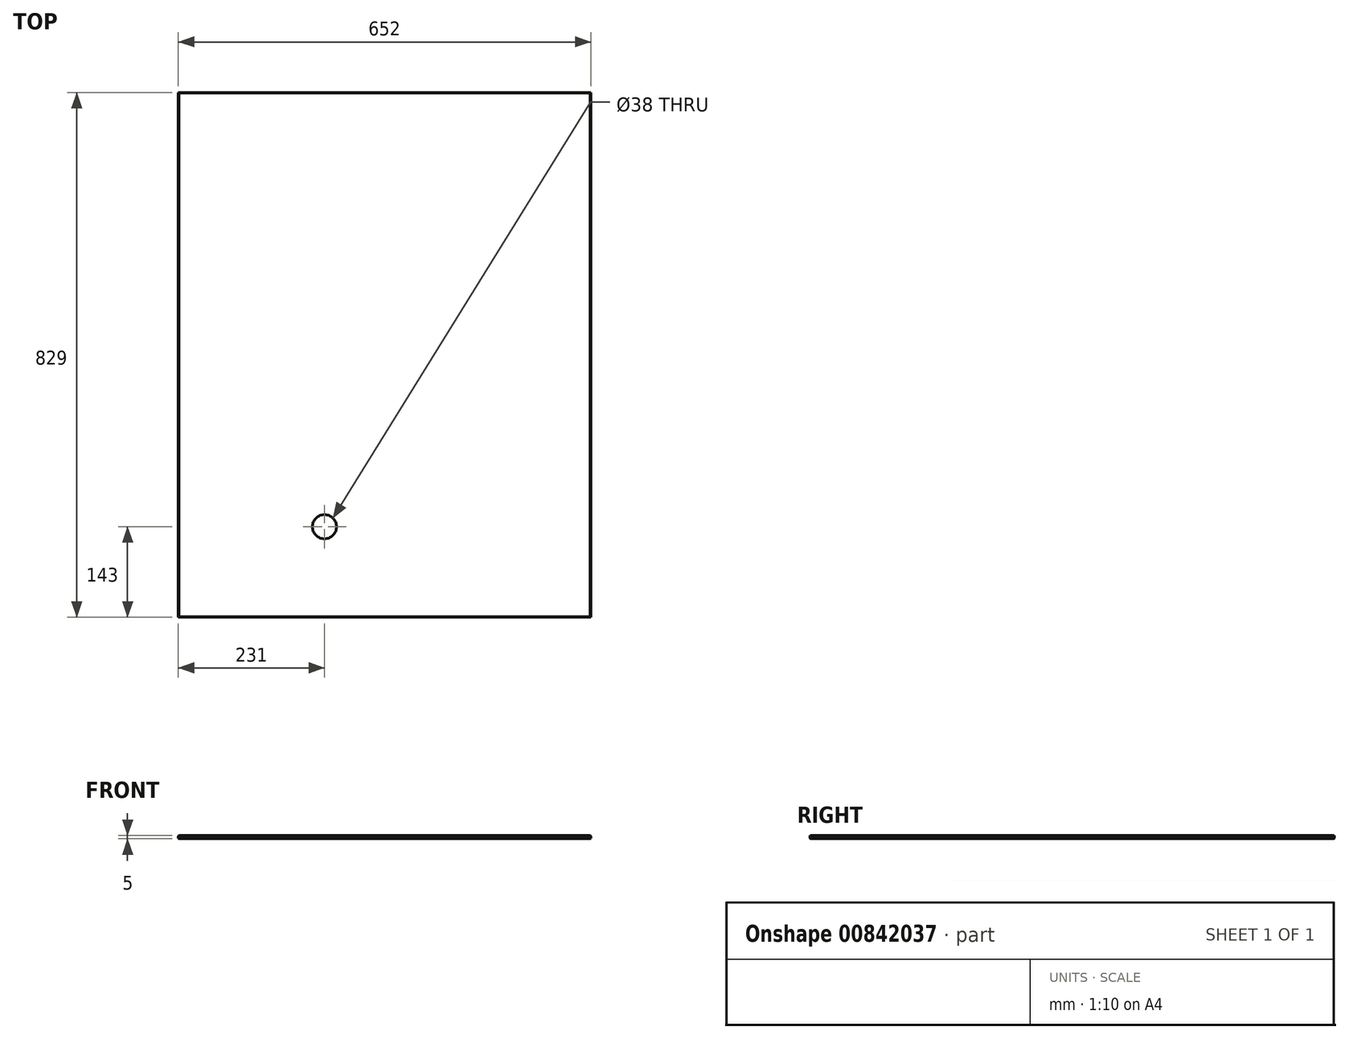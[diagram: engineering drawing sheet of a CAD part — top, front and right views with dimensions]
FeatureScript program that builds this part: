
annotation { "Feature Type Name" : "Feature", "Feature Type Description" : "" }
export const myFeature = defineFeature(function(context is Context, id is Id, definition is map)
    precondition{}
    {
        {
            var Q0;
            Q0=qCreatedBy(makeId("Top.planeOp"),FACE);
            var sketch = newSketch(context, id + "F0", { "sketchPlane" : qUnion([Q0])});
            skLineSegment(sketch, "E0.bottom", {"start": v(-326, 414.5) * mm, "end": v(326, 414.5) * mm});
            skLineSegment(sketch, "E0.top", {"start": v(-326, -414.5) * mm, "end": v(326, -414.5) * mm});
            skLineSegment(sketch, "E0.left", {"start": v(-326, 414.5) * mm, "end": v(-326, -414.5) * mm});
            skLineSegment(sketch, "E0.right", {"start": v(326, 414.5) * mm, "end": v(326, -414.5) * mm});
            skPoint(sketch, "E0.middle", {"position": v(0, 0) * mm});
            skSolve(sketch);
        }
        {
            var Q0;
            Q0=makeQuery(id+"F0.imprint","IMPRINT",FACE,{"disambiguationData":[TD([[makeQuery(id+"F0.imprint","IMPRINT",EDGE,{"derivedFrom":sQuery(id+"F0.wireOp",EDGE,"E0.bottom")}),-1.0]])]});
            extrude(context, id + "F1", {"entities" : qUnion([Q0]), "endBound" : BoundingType.SYMMETRIC, "depth" : 5 * mm, "offsetDistance" : 25 * mm});
        }
        {
            var Q0;
            Q0=makeQuery(id+"F1.opExtrude","CAP_FACE",FACE,{"disambiguationData":[OSD([sQuery(id+"F0.wireOp",EDGE,"E0.bottom"),sQuery(id+"F0.wireOp",EDGE,"E0.top"),sQuery(id+"F0.wireOp",EDGE,"E0.left"),sQuery(id+"F0.wireOp",EDGE,"E0.right")])],"isStart":false});
            var sketch = newSketch(context, id + "F2", { "sketchPlane" : qUnion([Q0])});
            skPoint(sketch, "E1", {"position": v(-95, -271.5) * mm});
            skSolve(sketch);
        }
        {
            var Q0;
            Q0=sQuery(id+"F2.wireOp",VERTEX,"E1");
            var Q1;
            Q1=makeQuery(id+"F1.opExtrude","SWEPT_BODY",BODY,{"disambiguationData":[OSD([sQuery(id+"F0.wireOp",EDGE,"E0.bottom"),sQuery(id+"F0.wireOp",EDGE,"E0.top"),sQuery(id+"F0.wireOp",EDGE,"E0.left"),sQuery(id+"F0.wireOp",EDGE,"E0.right")])]});
            hole(context, id + "F3", {"style" : HoleStyle.SIMPLE, "endStyle" : HoleEndStyle.THROUGH, "holeDiameter" : 38 * mm, "majorDiameter" : 5 * mm, "isTappedThrough" : true, "tappedDepth" : 12 * mm, "tapClearance" : 3, "locations" : qUnion([Q0]), "scope" : qUnion([Q1])});
        }
        {
            var Q0;
            Q0=makeQuery(id+"F1.opExtrude","CAP_EDGE",EDGE,{"disambiguationData":[OSD([sQuery(id+"F0.wireOp",EDGE,"E0.top")])],"isStart":true});
            var Q1;
            Q1=makeQuery(id+"F1.opExtrude","CAP_EDGE",EDGE,{"disambiguationData":[OSD([sQuery(id+"F0.wireOp",EDGE,"E0.left")])],"isStart":true});
            var Q2;
            Q2=makeQuery(id+"F1.opExtrude","CAP_EDGE",EDGE,{"disambiguationData":[OSD([sQuery(id+"F0.wireOp",EDGE,"E0.bottom")])],"isStart":true});
            var Q3;
            Q3=makeQuery(id+"F1.opExtrude","CAP_EDGE",EDGE,{"disambiguationData":[OSD([sQuery(id+"F0.wireOp",EDGE,"E0.right")])],"isStart":true});
            var Q4;
            Q4=makeQuery(id+"F1.opExtrude","CAP_EDGE",EDGE,{"disambiguationData":[OSD([sQuery(id+"F0.wireOp",EDGE,"E0.right")])],"isStart":false});
            var Q5;
            Q5=makeQuery(id+"F1.opExtrude","CAP_EDGE",EDGE,{"disambiguationData":[OSD([sQuery(id+"F0.wireOp",EDGE,"E0.bottom")])],"isStart":false});
            var Q6;
            Q6=makeQuery(id+"F1.opExtrude","CAP_EDGE",EDGE,{"disambiguationData":[OSD([sQuery(id+"F0.wireOp",EDGE,"E0.left")])],"isStart":false});
            var Q7;
            Q7=makeQuery(id+"F1.opExtrude","CAP_EDGE",EDGE,{"disambiguationData":[OSD([sQuery(id+"F0.wireOp",EDGE,"E0.top")])],"isStart":false});
            chamfer(context, id + "F4", {"entities" : qUnion([Q0, Q1, Q2, Q3, Q4, Q5, Q6, Q7]), "width" : 1 * mm, "tangentPropagation" : true});
        }
    });
